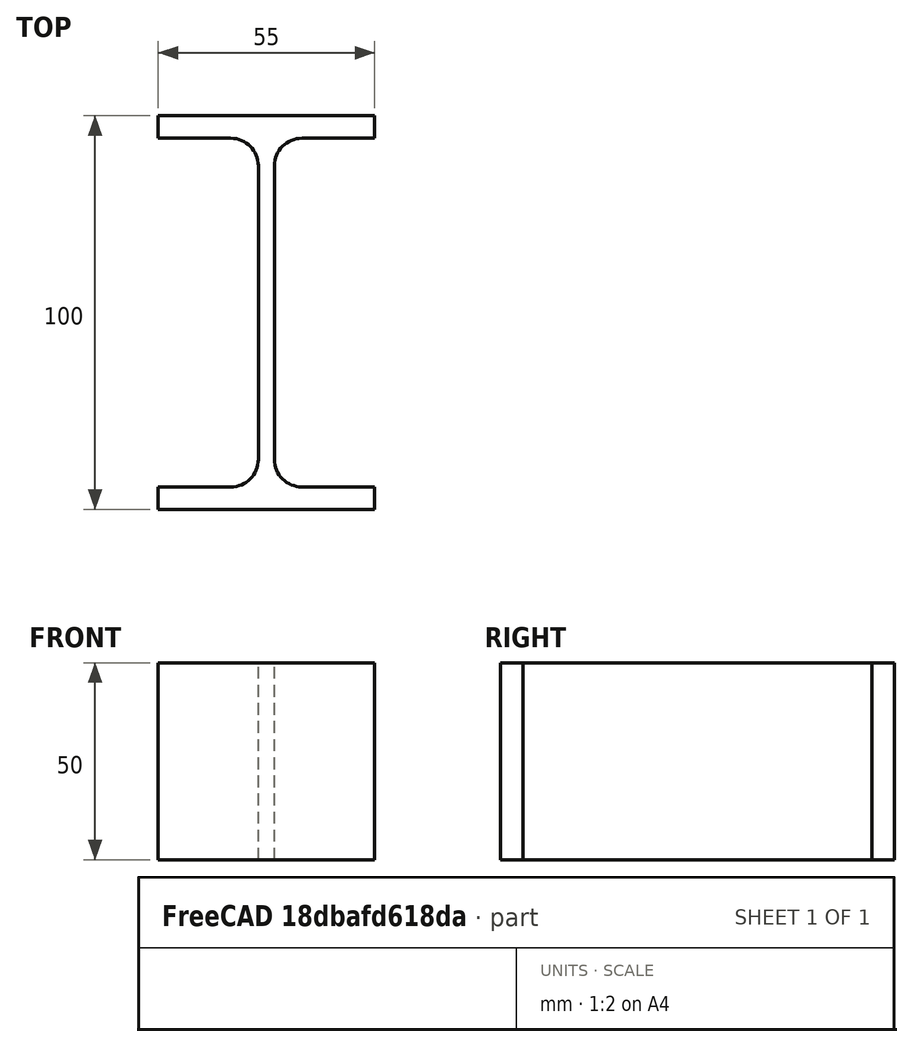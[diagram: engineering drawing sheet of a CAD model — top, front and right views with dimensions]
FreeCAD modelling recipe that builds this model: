
FCSTD DOCUMENT  (FreeCAD 0.15R4671 (Git))
Label: IPE-Profile 100 DIN1025-5 S235JR
License: All rights reserved
LicenseURL: http://en.wikipedia.org/wiki/All_rights_reserved
objects: Sketcher::SketchObject×1, Part::Extrusion×1
note: 2 computed .brp shape members not serialized (recipe doc carries the construction recipe); baked Part::Feature solids carry a one-line shape summary decoded from their .brp

FEATURE [Sketcher::SketchObject] Sketch
  sketch-geometry (16):
    g0: LineSegment StartX=2.05 StartY=-37.3 StartZ=0 EndX=2.05 EndY=37.3 EndZ=0
    g1: LineSegment StartX=9.05 StartY=44.3 StartZ=0 EndX=27.5 EndY=44.3 EndZ=0
    g2: LineSegment StartX=27.5 StartY=44.3 StartZ=0 EndX=27.5 EndY=50 EndZ=0
    g3: LineSegment StartX=27.5 StartY=50 StartZ=0 EndX=-27.5 EndY=50 EndZ=0
    g4: LineSegment StartX=-27.5 StartY=50 StartZ=0 EndX=-27.5 EndY=44.3 EndZ=0
    g5: LineSegment StartX=-27.5 StartY=44.3 StartZ=0 EndX=-9.05 EndY=44.3 EndZ=0
    g6: LineSegment StartX=-2.05 StartY=37.3 StartZ=0 EndX=-2.05 EndY=-37.3 EndZ=0
    g7: LineSegment StartX=-9.05 StartY=-44.3 StartZ=0 EndX=-27.5 EndY=-44.3 EndZ=0
    g8: LineSegment StartX=-27.5 StartY=-44.3 StartZ=0 EndX=-27.5 EndY=-50 EndZ=0
    g9: LineSegment StartX=-27.5 StartY=-50 StartZ=0 EndX=27.5 EndY=-50 EndZ=0
    g10: LineSegment StartX=27.5 StartY=-50 StartZ=0 EndX=27.5 EndY=-44.3 EndZ=0
    g11: LineSegment StartX=27.5 StartY=-44.3 StartZ=0 EndX=9.05 EndY=-44.3 EndZ=0
    g12: ArcOfCircle CenterX=9.05 CenterY=37.3 CenterZ=0 NormalX=0 NormalY=0 NormalZ=1 Radius=7 StartAngle=1.5708 EndAngle=3.14159
    g13: ArcOfCircle CenterX=9.05 CenterY=-37.3 CenterZ=0 NormalX=0 NormalY=0 NormalZ=1 Radius=7 StartAngle=3.14159 EndAngle=4.71239
    g14: ArcOfCircle CenterX=-9.05 CenterY=37.3 CenterZ=0 NormalX=0 NormalY=0 NormalZ=1 Radius=7 StartAngle=0 EndAngle=1.5708
    g15: ArcOfCircle CenterX=-9.05 CenterY=-37.3 CenterZ=0 NormalX=0 NormalY=0 NormalZ=1 Radius=7 StartAngle=4.71239 EndAngle=6.28319
  constraints (42):
    c: Vertical(g0)
    c: Coincident(g2,g1)
    c: Vertical(g2)
    c: Coincident(g3,g2)
    c: Coincident(g4,g3)
    c: Vertical(g4)
    c: Coincident(g5,g4)
    c: Horizontal(g5)
    c: Vertical(g6)
    c: Horizontal(g7)
    c: Coincident(g8,g7)
    c: Vertical(g8)
    c: Coincident(g9,g8)
    c: Horizontal(g9)
    c: Coincident(g10,g9)
    c: Vertical(g10)
    c: Coincident(g11,g10)
    c: Horizontal(g11)
    c: Tangent(g1,g12) = 1.5708
    c: Tangent(g0,g12) = 1.5708
    c: Tangent(g0,g13) = 1.5708
    c: Tangent(g11,g13) = 1.5708
    c: Tangent(g5,g14) = 1.5708
    c: Tangent(g6,g14) = 1.5708
    c: Tangent(g6,g15) = 1.5708
    c: Tangent(g7,g15) = 1.5708
    c: Equal(g3,g9)
    c: Equal(g2,g4)
    c: Equal(g4,g8)
    c: Equal(g8,g10)
    c: Equal(g12,g14)
    c: Equal(g14,g15)
    c: Equal(g15,g13)
    c: Symmetric(g2,g3,g-2)
    c: Symmetric(g9,g8,g-2)
    c: Symmetric(g0,g6,g-2)
    c: Symmetric(g2,g9,g-1)
    c: DistanceY(g2,g9) = -100
    c: DistanceX(g3) = -55
    c: DistanceX(g0,g6) = -4.1
    c: DistanceY(g2) = 5.7
    c: Radius(g12) = 7
FEATURE [Part::Extrusion] Extrude  label="IPE-Profile 100 DIN1025-5 S235JR"
  Base = -> Sketch
  Dir = (0,0,50)
  Solid = true
